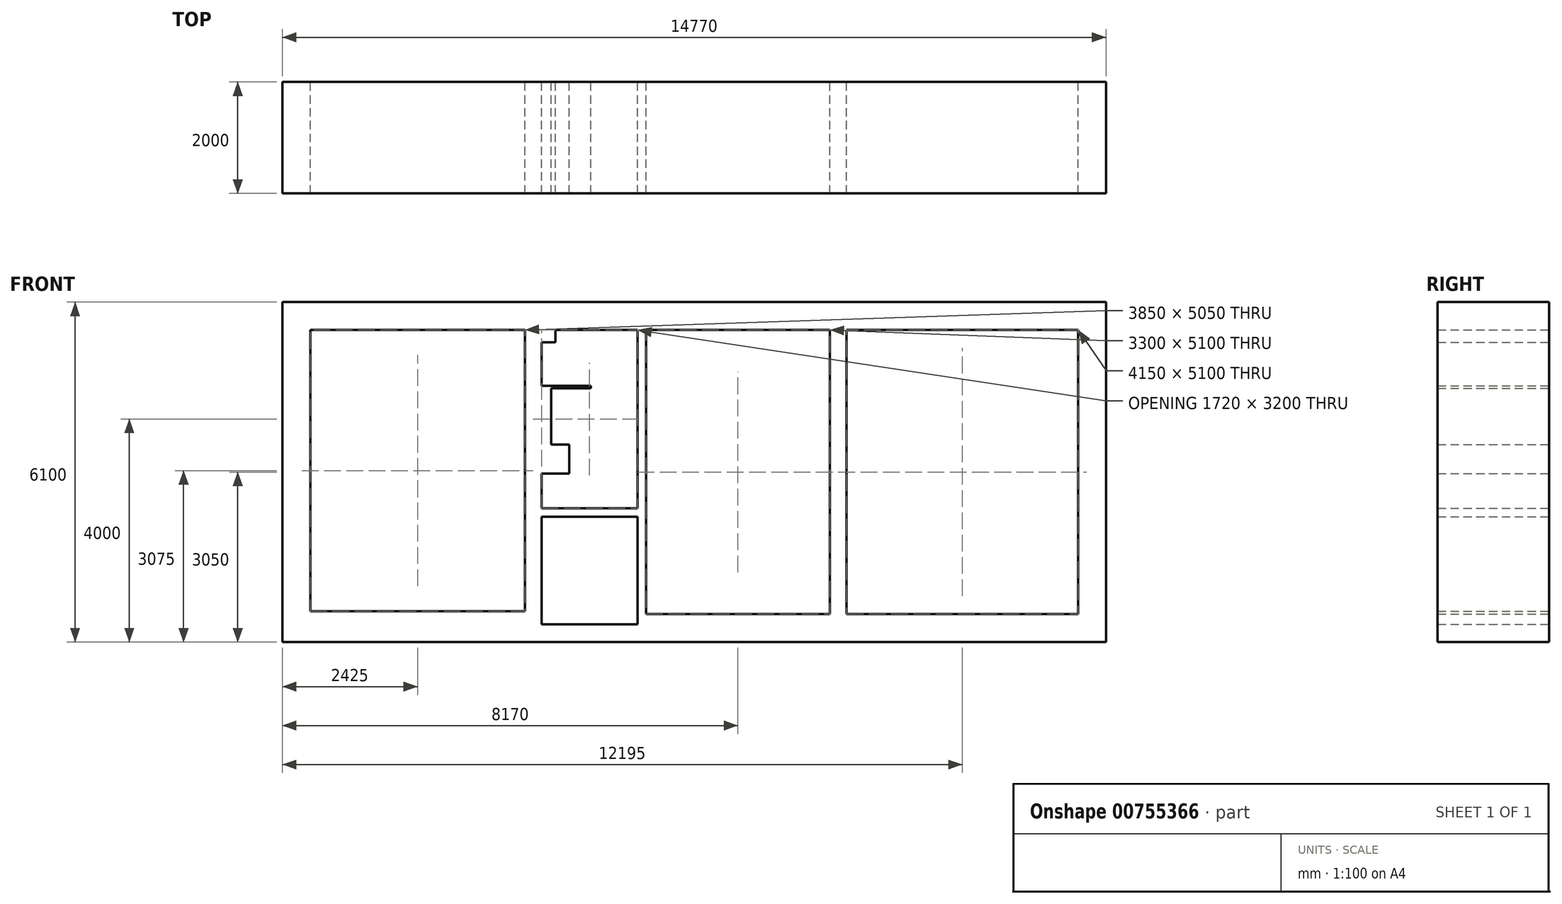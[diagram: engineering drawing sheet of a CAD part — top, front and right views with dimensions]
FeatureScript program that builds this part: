
annotation { "Feature Type Name" : "Feature", "Feature Type Description" : "" }
export const myFeature = defineFeature(function(context is Context, id is Id, definition is map)
    precondition{}
    {
        {
            var Q0;
            Q0=qCreatedBy(makeId("Front.planeOp"),FACE);
            var sketch = newSketch(context, id + "F0", { "sketchPlane" : qUnion([Q0])});
            skLineSegment(sketch, "E0.bottom", {"start": v(1052.84, 0) * mm, "end": v(2772.84, 0) * mm});
            skLineSegment(sketch, "E0.top", {"start": v(1302.84, 3200) * mm, "end": v(2772.84, 3200) * mm});
            skLineSegment(sketch, "E0.right", {"start": v(2772.84, 0) * mm, "end": v(2772.84, 3200) * mm});
            skLineSegment(sketch, "E1", {"start": v(1302.84, 3200) * mm, "end": v(1302.84, 2980) * mm});
            skLineSegment(sketch, "E2", {"start": v(1302.84, 2980) * mm, "end": v(1052.84, 2980) * mm});
            skLineSegment(sketch, "E3", {"start": v(1052.84, 2980) * mm, "end": v(1052.84, 2200) * mm});
            skLineSegment(sketch, "E4", {"start": v(1052.84, 2200) * mm, "end": v(1932.84, 2200) * mm});
            skLineSegment(sketch, "E5", {"start": v(1932.84, 2200) * mm, "end": v(1932.84, 2150) * mm});
            skLineSegment(sketch, "E6", {"start": v(1225.5, 2150) * mm, "end": v(1225.5, 1140) * mm});
            skLineSegment(sketch, "E7", {"start": v(1225.5, 1140) * mm, "end": v(1545.5, 1140) * mm});
            skLineSegment(sketch, "E8", {"start": v(1545.5, 1140) * mm, "end": v(1545.5, 620) * mm});
            skLineSegment(sketch, "E9", {"start": v(1545.5, 620) * mm, "end": v(1052.84, 620) * mm});
            skLineSegment(sketch, "E10.bottom", {"start": v(1052.84, -150) * mm, "end": v(2772.84, -150) * mm});
            skLineSegment(sketch, "E10.top", {"start": v(1052.84, -2080) * mm, "end": v(2772.84, -2080) * mm});
            skLineSegment(sketch, "E10.left", {"start": v(1052.84, -150) * mm, "end": v(1052.84, -2080) * mm});
            skLineSegment(sketch, "E10.right", {"start": v(2772.84, -150) * mm, "end": v(2772.84, -2080) * mm});
            skLineSegment(sketch, "E11.bottom", {"start": v(752.84, -1850) * mm, "end": v(-3097.16, -1850) * mm});
            skLineSegment(sketch, "E11.top", {"start": v(752.84, 3200) * mm, "end": v(-3097.16, 3200) * mm});
            skLineSegment(sketch, "E11.left", {"start": v(752.84, -1850) * mm, "end": v(752.84, 3200) * mm});
            skLineSegment(sketch, "E11.right", {"start": v(-3097.16, -1850) * mm, "end": v(-3097.16, 3200) * mm});
            skLineSegment(sketch, "E12.bottom", {"start": v(2922.84, 3200) * mm, "end": v(6222.84, 3200) * mm});
            skLineSegment(sketch, "E12.top", {"start": v(2922.84, -1900) * mm, "end": v(6222.84, -1900) * mm});
            skLineSegment(sketch, "E12.left", {"start": v(2922.84, 3200) * mm, "end": v(2922.84, -1900) * mm});
            skLineSegment(sketch, "E12.right", {"start": v(6222.84, 3200) * mm, "end": v(6222.84, -1900) * mm});
            skLineSegment(sketch, "E13.bottom", {"start": v(6522.84, 3200) * mm, "end": v(10672.84, 3200) * mm});
            skLineSegment(sketch, "E13.top", {"start": v(6522.84, -1900) * mm, "end": v(10672.84, -1900) * mm});
            skLineSegment(sketch, "E13.left", {"start": v(6522.84, 3200) * mm, "end": v(6522.84, -1900) * mm});
            skLineSegment(sketch, "E13.right", {"start": v(10672.84, 3200) * mm, "end": v(10672.84, -1900) * mm});
            skLineSegment(sketch, "E14.bottom", {"start": v(-3597.16, 3700) * mm, "end": v(11172.84, 3700) * mm});
            skLineSegment(sketch, "E14.top", {"start": v(-3597.16, -2400) * mm, "end": v(11172.84, -2400) * mm});
            skLineSegment(sketch, "E14.left", {"start": v(-3597.16, 3700) * mm, "end": v(-3597.16, -2400) * mm});
            skLineSegment(sketch, "E14.right", {"start": v(11172.84, 3700) * mm, "end": v(11172.84, -2400) * mm});
            skLineSegment(sketch, "E15", {"start": v(1052.84, 0) * mm, "end": v(1052.84, 620) * mm});
            skPoint(sketch, "E16.orphan", {"position": v(521.44, 620) * mm});
            skLineSegment(sketch, "E17", {"start": v(1932.84, 2150) * mm, "end": v(1225.5, 2150) * mm});
            skSolve(sketch);
        }
        {
            var Q0;
            Q0=makeQuery(id+"F0.imprint","IMPRINT",FACE,{"disambiguationData":[TD([[makeQuery(id+"F0.imprint","IMPRINT",EDGE,{"derivedFrom":sQuery(id+"F0.wireOp",EDGE,"E0.bottom")}),-1.0]])]});
            extrude(context, id + "F1", {"entities" : qUnion([Q0]), "depth" : 2000 * mm, "offsetDistance" : 25 * mm});
        }
    });
